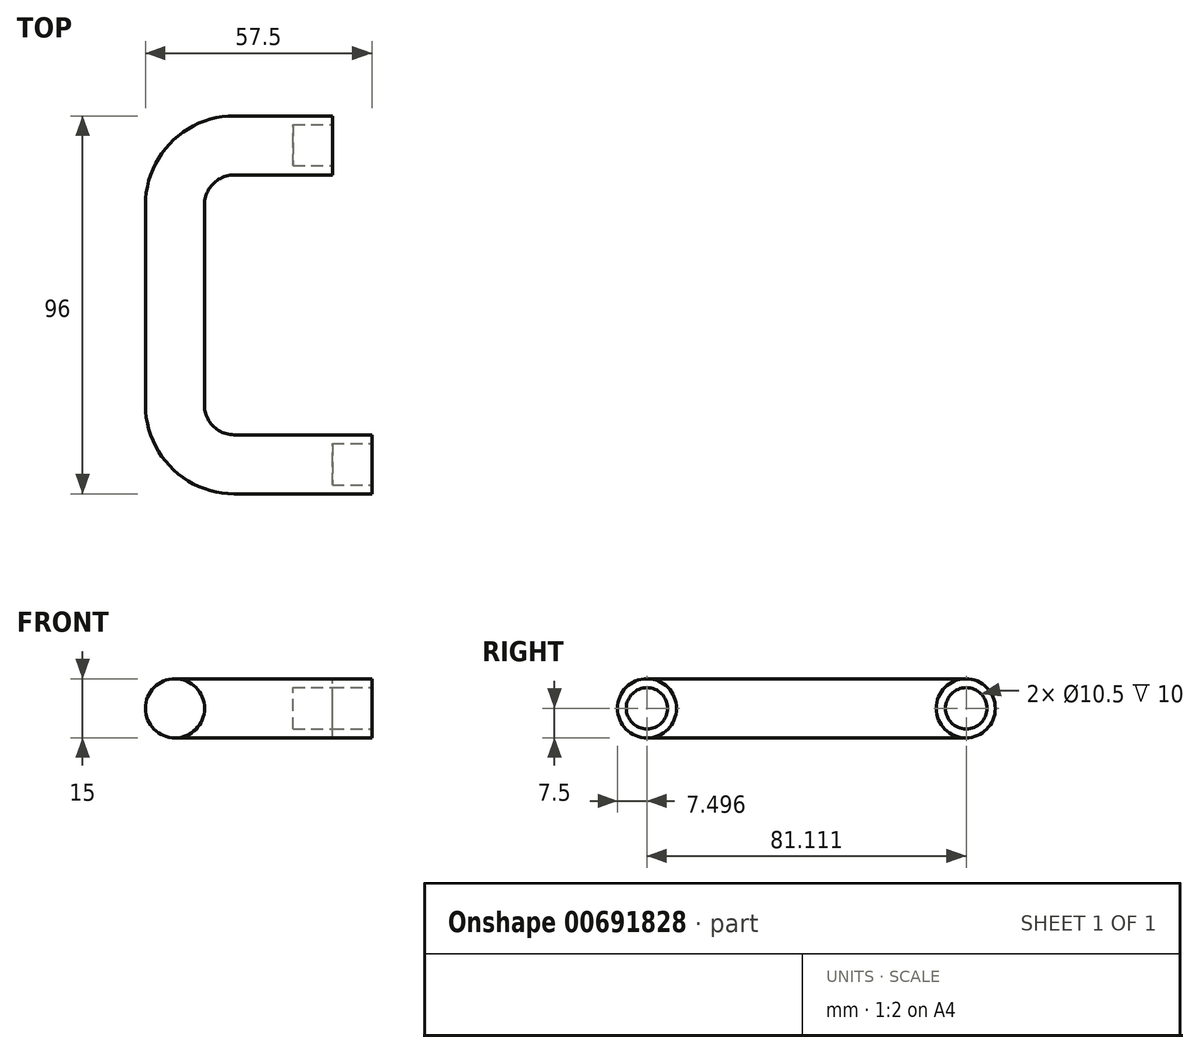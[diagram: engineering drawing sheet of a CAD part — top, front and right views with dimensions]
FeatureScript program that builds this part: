
annotation { "Feature Type Name" : "Feature", "Feature Type Description" : "" }
export const myFeature = defineFeature(function(context is Context, id is Id, definition is map)
    precondition{}
    {
        {
            var Q0;
            Q0=qCreatedBy(makeId("Right.planeOp"),FACE);
            var sketch = newSketch(context, id + "F0", { "sketchPlane" : qUnion([Q0])});
            skCircle(sketch, "E0", {"center": v(-20.43, 0) * mm, "radius": 7.5 * mm});
            skCircle(sketch, "E1", {"center": v(60.57, 0) * mm, "radius": 7.5 * mm});
            skSolve(sketch);
        }
        {
            var Q0;
            Q0=qCreatedBy(makeId("Top.planeOp"),FACE);
            var sketch = newSketch(context, id + "F1", { "sketchPlane" : qUnion([Q0])});
            skLineSegment(sketch, "E2", {"start": v(0, -20.43) * mm, "end": v(-25, -20.43) * mm});
            skLineSegment(sketch, "E3", {"start": v(-40, -5.43) * mm, "end": v(-40, 45.57) * mm});
            skLineSegment(sketch, "E4", {"start": v(-25, 60.57) * mm, "end": v(0, 60.57) * mm});
            skPoint(sketch, "E5.visualSharp", {"position": v(-40, 60.57) * mm});
            skArc(sketch, "E5.filletArc", {"start": v(-25, 60.57) * mm, "mid": v(-35.6, 56.17) * mm, "end": v(-40, 45.57) * mm});
            skPoint(sketch, "E6.visualSharp", {"position": v(-40, -20.43) * mm});
            skArc(sketch, "E6.filletArc", {"start": v(-40, -5.43) * mm, "mid": v(-35.6, -16.04) * mm, "end": v(-25, -20.43) * mm});
            skSolve(sketch);
        }
        {
            var Q0;
            Q0=makeQuery(id+"F0.imprint","IMPRINT",FACE,{"disambiguationData":[TD([[makeQuery(id+"F0.imprint","IMPRINT",EDGE,{"derivedFrom":sQuery(id+"F0.wireOp",EDGE,"E1")}),1.0]])]});
            var Q1;
            Q1=sQuery(id+"F1.wireOp",EDGE,"E2");
            var Q2;
            Q2=sQuery(id+"F1.wireOp",EDGE,"E6.filletArc");
            var Q3;
            Q3=sQuery(id+"F1.wireOp",EDGE,"E3");
            var Q4;
            Q4=sQuery(id+"F1.wireOp",EDGE,"E5.filletArc");
            var Q5;
            Q5=sQuery(id+"F1.wireOp",EDGE,"E4");
            sweep(context, id + "F2", {"profiles" : qUnion([Q0]), "path" : qUnion([Q1, Q2, Q3, Q4, Q5])});
        }
        {
            var Q0;
            Q0=makeQuery(id+"F0.imprint","IMPRINT",FACE,{"disambiguationData":[TD([[makeQuery(id+"F0.imprint","IMPRINT",EDGE,{"derivedFrom":sQuery(id+"F0.wireOp",EDGE,"E0")}),1.0]])]});
            var sketch = newSketch(context, id + "F3", { "sketchPlane" : qUnion([Q0])});
            skCircle(sketch, "E7.0", {"center": v(-20.43, 0) * mm, "radius": 7.5 * mm});
            skSolve(sketch);
        }
        {
            var Q0;
            Q0=qSketchRegion(id+"F3",true);
            extrude(context, id + "F4", {"entities" : qUnion([Q0]), "operationType" : NewBodyOperationType.ADD, "depth" : 10 * mm, "offsetDistance" : 25 * mm});
        }
        {
            var Q0;
            Q0=makeQuery(id+"F4.opExtrude","CAP_FACE",FACE,{"disambiguationData":[OSD([sQuery(id+"F3.wireOp",EDGE,"E7.0")])],"isStart":false});
            var sketch = newSketch(context, id + "F5", { "sketchPlane" : qUnion([Q0])});
            skCircle(sketch, "E8", {"center": v(-20.43, 0) * mm, "radius": 5.25 * mm});
            skSolve(sketch);
        }
        {
            var Q0;
            Q0=qSketchRegion(id+"F5",true);
            extrude(context, id + "F6", {"entities" : qUnion([Q0]), "operationType" : NewBodyOperationType.REMOVE, "oppositeDirection" : true, "depth" : 10 * mm, "offsetDistance" : 25 * mm});
        }
        {
            var Q0;
            Q0=makeQuery(id+"F0.imprint","IMPRINT",FACE,{"disambiguationData":[TD([[makeQuery(id+"F0.imprint","IMPRINT",EDGE,{"derivedFrom":sQuery(id+"F0.wireOp",EDGE,"E1")}),1.0]])]});
            var sketch = newSketch(context, id + "F7", { "sketchPlane" : qUnion([Q0])});
            skCircle(sketch, "E9", {"center": v(60.68, 0) * mm, "radius": 5.25 * mm});
            skSolve(sketch);
        }
        {
            var Q0;
            Q0=qSketchRegion(id+"F7",true);
            extrude(context, id + "F8", {"entities" : qUnion([Q0]), "operationType" : NewBodyOperationType.REMOVE, "oppositeDirection" : true, "depth" : 10 * mm, "offsetDistance" : 25 * mm});
        }
    });
